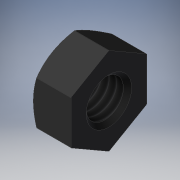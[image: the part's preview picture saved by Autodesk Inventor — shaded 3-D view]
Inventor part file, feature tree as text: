
AUTODESK INVENTOR PART (.ipt)
format: ipt  version: 2019 (Build 230136000, 136)  size: 157,184 bytes
history: native  units: mm
features: other x14, sketch x3, revolve x2, thread x1, extrude x1
ambient origin geometry x8: Origin, YZ Plane, XZ Plane, XY Plane, X Axis, Y Axis, Z Axis, Center Point
bodies: Solid1 (feature_tree)
feature tree (21):
  revolve  "Revolution1"  Angle=360.0deg
  revolve  "Revolution2"  [1 undecoded]
  thread  "Thread1"  [1 undecoded]
  extrude  "Extrusion1"  [1 undecoded]
  other  "cp_XY"
  other  "cp_YZ"
  other  "cp_ZX"
  other  "cp_X"
  other  "cp_Y"
  other  "cp_Z"
  other  "cp_Center"
  other  "nut_to_screw_XY"
  other  "nut_to_screw_YZ"
  other  "nut_to_screw_ZX"
  other  "nut_to_screw_X"
  other  "nut_to_screw_Y"
  other  "nut_to_screw_Z"
  other  "nut_to_screw_Center"
  sketch  "Sketch_1"  dims[d0=360.0deg d1=360.0deg]
  sketch  "Sketch_2"  dims[d2=3.917mm d3=0.0mm d4=5.0mm d5=0.0mm d6=0.0mm]
  sketch  "Sketch_3"
note: 3 required parameter values undecoded (feature->parameter linkage not recoverable at this tier; creation-order binding heuristic only, values carry confidence <= 0.55)